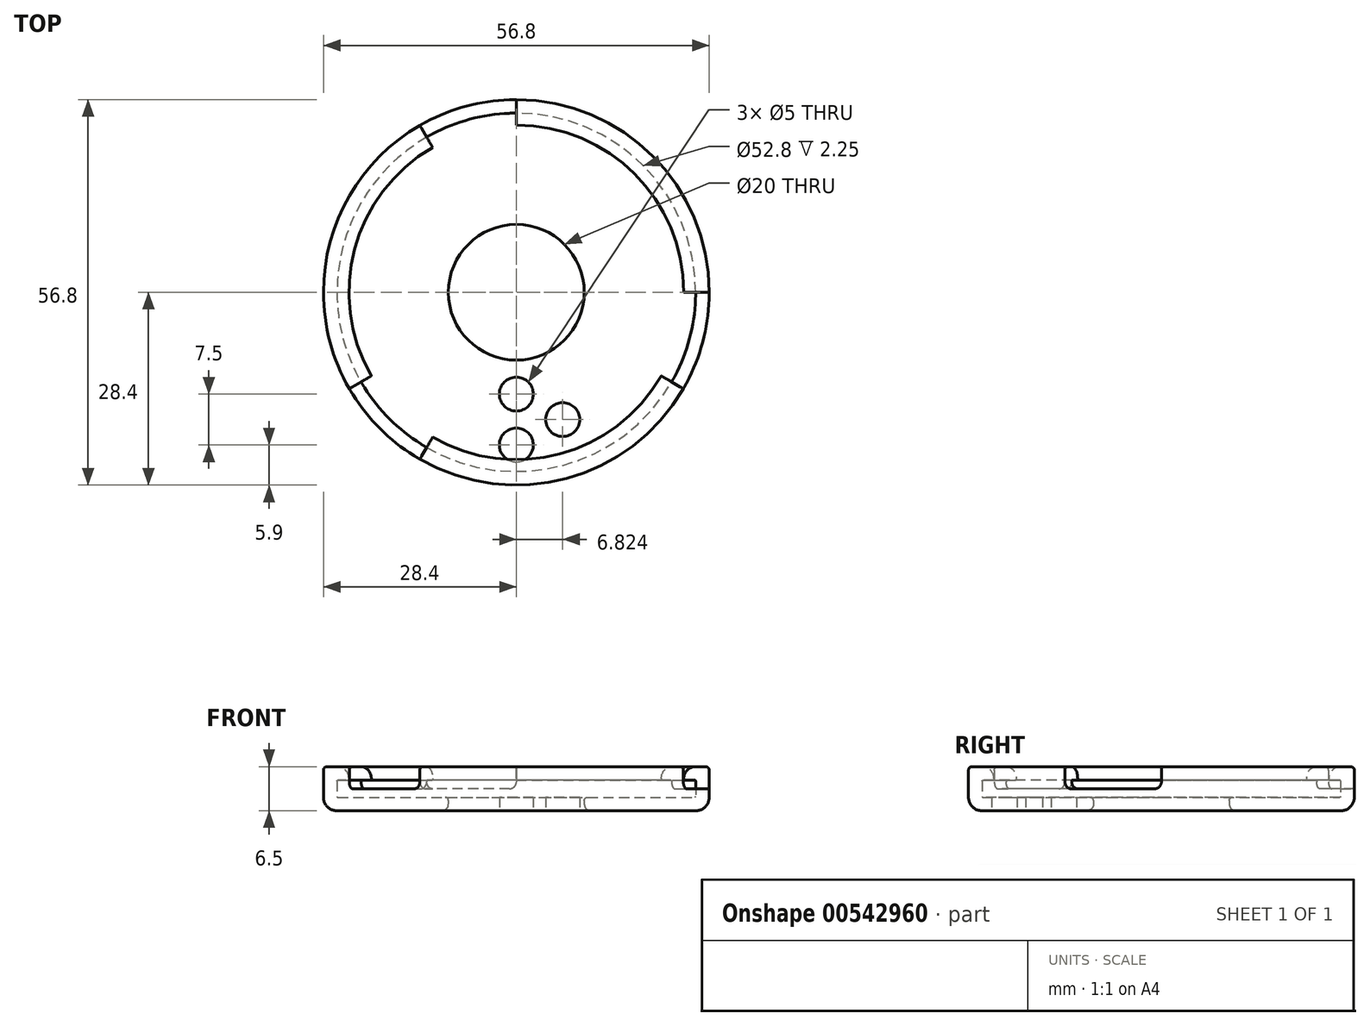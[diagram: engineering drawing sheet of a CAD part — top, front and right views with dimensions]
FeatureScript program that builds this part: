
annotation { "Feature Type Name" : "Feature", "Feature Type Description" : "" }
export const myFeature = defineFeature(function(context is Context, id is Id, definition is map)
    precondition{}
    {
        {
            var Q0;
            Q0=qCreatedBy(makeId("Front.planeOp"),FACE);
            var sketch = newSketch(context, id + "F0", { "sketchPlane" : qUnion([Q0])});
            skLineSegment(sketch, "E0", {"start": v(11, 0) * mm, "end": v(26.4, 0) * mm});
            skLineSegment(sketch, "E1", {"start": v(28.4, 2) * mm, "end": v(28.4, 6) * mm});
            skLineSegment(sketch, "E2", {"start": v(27.9, 6.5) * mm, "end": v(26.4, 6.5) * mm});
            skLineSegment(sketch, "E3", {"start": v(24.65, 4.75) * mm, "end": v(24.65, 4.63) * mm});
            skLineSegment(sketch, "E4", {"start": v(24.77, 4.5) * mm, "end": v(26.27, 4.5) * mm});
            skLineSegment(sketch, "E5", {"start": v(26.4, 4.38) * mm, "end": v(26.4, 2.13) * mm});
            skLineSegment(sketch, "E6", {"start": v(26.27, 2) * mm, "end": v(10.5, 2) * mm});
            skLineSegment(sketch, "E7", {"start": v(10, 1.5) * mm, "end": v(10, 1) * mm});
            skPoint(sketch, "E8.visualSharp", {"position": v(28.4, 0) * mm});
            skArc(sketch, "E8.filletArc", {"start": v(26.4, 0) * mm, "mid": v(27.81, 0.59) * mm, "end": v(28.4, 2) * mm});
            skPoint(sketch, "E9.visualSharp", {"position": v(28.4, 6.5) * mm});
            skArc(sketch, "E9.filletArc", {"start": v(28.4, 6) * mm, "mid": v(28.25, 6.35) * mm, "end": v(27.9, 6.5) * mm});
            skPoint(sketch, "E10.visualSharp", {"position": v(10, 0) * mm});
            skArc(sketch, "E10.filletArc", {"start": v(10, 1) * mm, "mid": v(10.3, 0.3) * mm, "end": v(11, 0) * mm});
            skPoint(sketch, "E11.visualSharp", {"position": v(10, 2) * mm});
            skArc(sketch, "E11.filletArc", {"start": v(10.5, 2) * mm, "mid": v(10.15, 1.85) * mm, "end": v(10, 1.5) * mm});
            skPoint(sketch, "E12.visualSharp", {"position": v(24.65, 6.5) * mm});
            skArc(sketch, "E12.filletArc", {"start": v(26.4, 6.5) * mm, "mid": v(25.16, 5.99) * mm, "end": v(24.65, 4.75) * mm});
            skPoint(sketch, "E13.visualSharp", {"position": v(24.65, 4.5) * mm});
            skArc(sketch, "E13.filletArc", {"start": v(24.65, 4.63) * mm, "mid": v(24.69, 4.54) * mm, "end": v(24.77, 4.5) * mm});
            skArc(sketch, "E14.filletArc", {"start": v(26.27, 2) * mm, "mid": v(26.36, 2.04) * mm, "end": v(26.4, 2.13) * mm});
            skPoint(sketch, "E15.visualSharp", {"position": v(26.4, 4.5) * mm});
            skArc(sketch, "E15.filletArc", {"start": v(26.4, 4.38) * mm, "mid": v(26.36, 4.46) * mm, "end": v(26.27, 4.5) * mm});
            skSolve(sketch);
        }
        {
            var Q0;
            Q0=qCreatedBy(makeId("Front.planeOp"),FACE);
            var sketch = newSketch(context, id + "F1", { "sketchPlane" : qUnion([Q0])});
            skLineSegment(sketch, "E16", {"start": v(0, 0) * mm, "end": v(0, 35.52) * mm, "construction": true});
            skSolve(sketch);
        }
        {
            var Q0;
            Q0=makeQuery(id+"F0.imprint","IMPRINT",FACE,{"disambiguationData":[TD([[makeQuery(id+"F0.imprint","IMPRINT",EDGE,{"derivedFrom":sQuery(id+"F0.wireOp",EDGE,"E0")}),1.0]])]});
            var Q1;
            Q1=sQuery(id+"F1.wireOp",EDGE,"E16");
            revolve(context, id + "F2", {"entities" : qUnion([Q0]), "axis" : qUnion([Q1]), "revolveType" : RevolveType.FULL});
        }
        {
            var Q0;
            Q0=makeQuery(id+"F2.opRevolve","SWEPT_FACE",FACE,{"disambiguationData":[OSD([sQuery(id+"F0.wireOp",EDGE,"E0")])]});
            var sketch = newSketch(context, id + "F3", { "sketchPlane" : qUnion([Q0])});
            skCircle(sketch, "E17", {"center": v(0, 15) * mm, "radius": 2.5 * mm});
            skCircle(sketch, "E18", {"center": v(6.82, 18.75) * mm, "radius": 2.5 * mm});
            skLineSegment(sketch, "E19", {"start": v(6.82, 18.75) * mm, "end": v(0, 0) * mm, "construction": true});
            skLineSegment(sketch, "E20", {"start": v(0, 0) * mm, "end": v(0, 31.7) * mm, "construction": true});
            skCircle(sketch, "E21", {"center": v(0, 22.5) * mm, "radius": 2.5 * mm});
            skLineSegment(sketch, "E22", {"start": v(0, 22.5) * mm, "end": v(6.82, 18.75) * mm, "construction": true});
            skLineSegment(sketch, "E23", {"start": v(6.82, 18.75) * mm, "end": v(0, 15) * mm, "construction": true});
            skSolve(sketch);
        }
        {
            var Q0;
            Q0=makeQuery(id+"F3.imprint","IMPRINT",FACE,{"disambiguationData":[TD([[makeQuery(id+"F3.imprint","IMPRINT",EDGE,{"derivedFrom":sQuery(id+"F3.wireOp",EDGE,"E21")}),1.0]])]});
            var Q1;
            Q1=makeQuery(id+"F3.imprint","IMPRINT",FACE,{"disambiguationData":[TD([[makeQuery(id+"F3.imprint","IMPRINT",EDGE,{"derivedFrom":sQuery(id+"F3.wireOp",EDGE,"E18")}),1.0]])]});
            var Q2;
            Q2=makeQuery(id+"F3.imprint","IMPRINT",FACE,{"disambiguationData":[TD([[makeQuery(id+"F3.imprint","IMPRINT",EDGE,{"derivedFrom":sQuery(id+"F3.wireOp",EDGE,"E17")}),1.0]])]});
            extrude(context, id + "F4", {"entities" : qUnion([Q0, Q1, Q2]), "operationType" : NewBodyOperationType.REMOVE, "endBound" : BoundingType.UP_TO_NEXT, "oppositeDirection" : true, "depth" : 25 * mm, "offsetDistance" : 25 * mm});
        }
        {
            var Q0;
            Q0=makeQuery(id+"F2.opRevolve","SWEPT_FACE",FACE,{"disambiguationData":[OSD([sQuery(id+"F0.wireOp",EDGE,"E6")])]});
            cPlane(context, id + "F5", {"entities" : qUnion([Q0]), "cplaneType" : CPlaneType.OFFSET, "offset" : 1.25 * mm, "width" : 150 * mm, "height" : 150 * mm});
        }
        {
            var Q0;
            Q0=qCreatedBy(id+"F5.planeOp",FACE);
            var sketch = newSketch(context, id + "F6", { "sketchPlane" : qUnion([Q0])});
            skCircle(sketch, "E24.0", {"center": v(0, 0) * mm, "radius": 26.4 * mm, "construction": true});
            skLineSegment(sketch, "E25", {"start": v(0, 0) * mm, "end": v(0, 50) * mm});
            skLineSegment(sketch, "E26", {"start": v(50, 0) * mm, "end": v(0, 0) * mm});
            skLineSegment(sketch, "E27", {"start": v(0, 0) * mm, "end": v(43.3, -25) * mm});
            skLineSegment(sketch, "E28", {"start": v(-25, -43.3) * mm, "end": v(0, 0) * mm});
            skLineSegment(sketch, "E29", {"start": v(0, 0) * mm, "end": v(-43.3, -25) * mm});
            skLineSegment(sketch, "E30", {"start": v(-25, 43.3) * mm, "end": v(0, 0) * mm});
            skLineSegment(sketch, "E31", {"start": v(-25, 43.3) * mm, "end": v(0, 50) * mm});
            skLineSegment(sketch, "E32", {"start": v(50, 0) * mm, "end": v(43.3, -25) * mm});
            skLineSegment(sketch, "E33", {"start": v(-25, -43.3) * mm, "end": v(-43.3, -25) * mm});
            skSolve(sketch);
        }
        {
            var Q0;
            Q0=qSketchRegion(id+"F6",true);
            extrude(context, id + "F7", {"entities" : qUnion([Q0]), "operationType" : NewBodyOperationType.REMOVE, "depth" : 25 * mm, "offsetDistance" : 25 * mm});
        }
        {
            var Q0;
            Q0=makeQuery(id+"F7.boolean.opBoolean","COPY",EDGE,{"derivedFrom":makeQuery(id+"F7.opExtrude","CAP_EDGE",EDGE,{"disambiguationData":[OSD([sQuery(id+"F6.wireOp",EDGE,"E25")])],"isStart":true})});
            var Q1;
            Q1=makeQuery(id+"F7.boolean.opBoolean","COPY",EDGE,{"derivedFrom":makeQuery(id+"F7.opExtrude","CAP_EDGE",EDGE,{"disambiguationData":[OSD([sQuery(id+"F6.wireOp",EDGE,"E30")])],"isStart":true})});
            var Q2;
            Q2=makeQuery(id+"F7.boolean.opBoolean","COPY",EDGE,{"derivedFrom":makeQuery(id+"F7.opExtrude","CAP_EDGE",EDGE,{"disambiguationData":[OSD([sQuery(id+"F6.wireOp",EDGE,"E26")])],"isStart":true})});
            var Q3;
            Q3=makeQuery(id+"F7.boolean.opBoolean","COPY",EDGE,{"derivedFrom":makeQuery(id+"F7.opExtrude","CAP_EDGE",EDGE,{"disambiguationData":[OSD([sQuery(id+"F6.wireOp",EDGE,"E27")])],"isStart":true})});
            var Q4;
            Q4=makeQuery(id+"F7.boolean.opBoolean","COPY",EDGE,{"derivedFrom":makeQuery(id+"F7.opExtrude","CAP_EDGE",EDGE,{"disambiguationData":[OSD([sQuery(id+"F6.wireOp",EDGE,"E28")])],"isStart":true})});
            var Q5;
            Q5=makeQuery(id+"F7.boolean.opBoolean","COPY",EDGE,{"derivedFrom":makeQuery(id+"F7.opExtrude","CAP_EDGE",EDGE,{"disambiguationData":[OSD([sQuery(id+"F6.wireOp",EDGE,"E29")])],"isStart":true})});
            fillet(context, id + "F8", {"entities" : qUnion([Q0, Q1, Q2, Q3, Q4, Q5]), "radius" : 1 * mm, "tangentPropagation" : true, "allowEdgeOverflow" : false});
        }
    });
